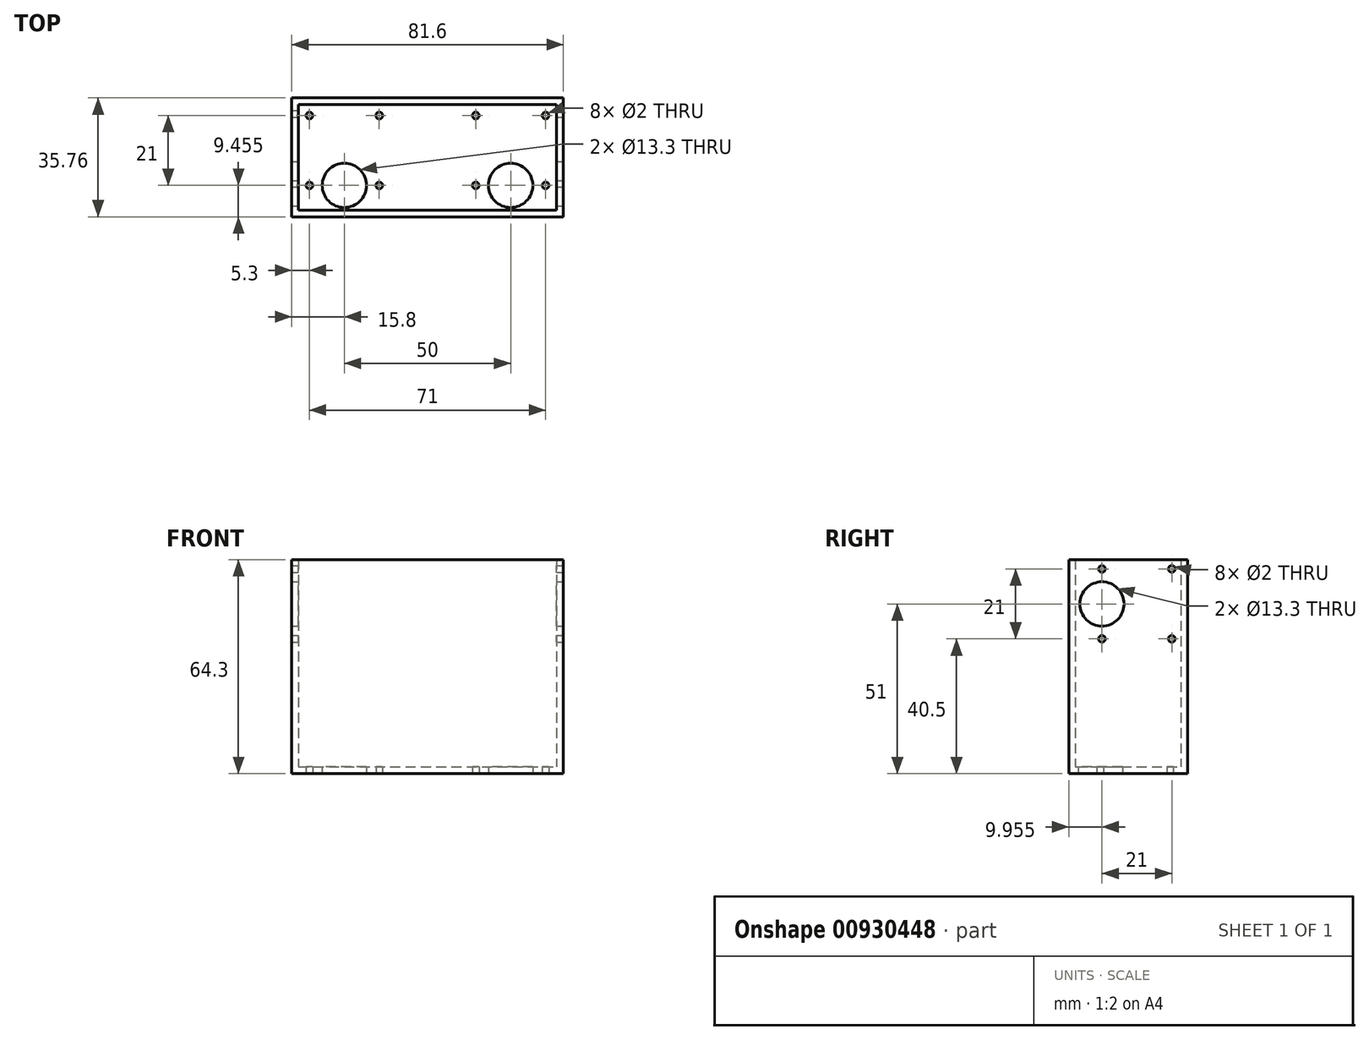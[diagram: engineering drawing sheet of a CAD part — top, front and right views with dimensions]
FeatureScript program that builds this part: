
annotation { "Feature Type Name" : "Feature", "Feature Type Description" : "" }
export const myFeature = defineFeature(function(context is Context, id is Id, definition is map)
    precondition{}
    {
        {
            var Q0;
            Q0=qCreatedBy(makeId("Top.planeOp"),FACE);
            var sketch = newSketch(context, id + "F0", { "sketchPlane" : qUnion([Q0])});
            skLineSegment(sketch, "E0.bottom", {"start": v(-40.8, 17.88) * mm, "end": v(40.8, 17.88) * mm});
            skLineSegment(sketch, "E0.top", {"start": v(-40.8, -17.88) * mm, "end": v(40.8, -17.88) * mm});
            skLineSegment(sketch, "E0.left", {"start": v(-40.8, 17.88) * mm, "end": v(-40.8, -17.88) * mm});
            skLineSegment(sketch, "E0.right", {"start": v(40.8, 17.88) * mm, "end": v(40.8, -17.88) * mm});
            skPoint(sketch, "E0.middle", {"position": v(0, 0) * mm});
            skLineSegment(sketch, "E1.bottom", {"start": v(14.5, 12.58) * mm, "end": v(35.5, 12.58) * mm, "construction": true});
            skLineSegment(sketch, "E1.top", {"start": v(14.5, -8.43) * mm, "end": v(35.5, -8.43) * mm, "construction": true});
            skLineSegment(sketch, "E1.left", {"start": v(14.5, 12.58) * mm, "end": v(14.5, -8.43) * mm, "construction": true});
            skLineSegment(sketch, "E1.right", {"start": v(35.5, 12.58) * mm, "end": v(35.5, -8.43) * mm, "construction": true});
            skPoint(sketch, "E1.middle", {"position": v(25, 2.07) * mm});
            skCircle(sketch, "E2", {"center": v(25, -8.43) * mm, "radius": 6.65 * mm});
            skPoint(sketch, "E3", {"position": v(25, -15.08) * mm});
            skCircle(sketch, "E4", {"center": v(14.5, 12.58) * mm, "radius": 1 * mm});
            skCircle(sketch, "E5.1.0", {"center": v(14.5, -8.43) * mm, "radius": 1 * mm});
            skCircle(sketch, "E5.2.0", {"center": v(35.5, -8.42) * mm, "radius": 1 * mm});
            skPoint(sketch, "E5.center", {"position": v(25, 2.08) * mm});
            skCircle(sketch, "E6.1.3.0", {"center": v(35.5, 12.58) * mm, "radius": 1 * mm});
            skCircle(sketch, "E7.MirrorC", {"center": v(-14.5, 12.58) * mm, "radius": 1 * mm});
            skCircle(sketch, "E8.MirrorC", {"center": v(-35.5, 12.58) * mm, "radius": 1 * mm});
            skCircle(sketch, "E9.MirrorC", {"center": v(-35.5, -8.42) * mm, "radius": 1 * mm});
            skCircle(sketch, "E10.MirrorC", {"center": v(-14.5, -8.43) * mm, "radius": 1 * mm});
            skCircle(sketch, "E11.MirrorC", {"center": v(-25, -8.43) * mm, "radius": 6.65 * mm});
            skLineSegment(sketch, "E12", {"start": v(-38.8, 15.87) * mm, "end": v(-38.8, -15.88) * mm});
            skLineSegment(sketch, "E13", {"start": v(-38.8, -15.88) * mm, "end": v(0, -15.88) * mm});
            skLineSegment(sketch, "E14", {"start": v(-38.8, 15.87) * mm, "end": v(0, 15.88) * mm});
            skLineSegment(sketch, "E15.MirrorCS", {"start": v(38.8, 15.87) * mm, "end": v(0, 15.88) * mm});
            skLineSegment(sketch, "E16.MirrorCS", {"start": v(38.8, 15.87) * mm, "end": v(38.8, -15.88) * mm});
            skLineSegment(sketch, "E17.MirrorCS", {"start": v(38.8, -15.88) * mm, "end": v(0, -15.88) * mm});
            skSolve(sketch);
        }
        {
            var Q0;
            Q0 = qSketchRegion(id + "F0", true);
            var Q1;
            Q1=makeQuery(id+"F0.imprint","IMPRINT",FACE,{"disambiguationData":[TD([[makeQuery(id+"F0.imprint","IMPRINT",EDGE,{"derivedFrom":sQuery(id+"F0.wireOp",EDGE,"E2")}),-1.0]])]});
            extrude(context, id + "F1", {"entities" : qUnion([Q0, Q1]), "depth" : 2 * mm, "offsetDistance" : 25 * mm});
        }
        {
            var Q0;
            Q0=makeQuery(id+"F0.imprint","IMPRINT",FACE,{"disambiguationData":[TD([[makeQuery(id+"F0.imprint","IMPRINT",EDGE,{"derivedFrom":sQuery(id+"F0.wireOp",EDGE,"E0.bottom")}),-1.0]])]});
            extrude(context, id + "F2", {"entities" : qUnion([Q0]), "operationType" : NewBodyOperationType.ADD, "depth" : (60 + 4.3) * mm, "offsetDistance" : 25 * mm});
        }
        {
            var Q0;
            {var subQ0=sQuery(id+"F0.wireOp",EDGE,"E0.right");Q0=makeQuery(id+"F2.boolean.opBoolean","MERGE",FACE,{"derivedFrom":[makeQuery(id+"F1.opExtrude","SWEPT_FACE",FACE,{"disambiguationData":[OSD([subQ0])]}),makeQuery(id+"F2.opExtrude","SWEPT_FACE",FACE,{"disambiguationData":[OSD([subQ0])]})]});}
            var sketch = newSketch(context, id + "F3", { "sketchPlane" : qUnion([Q0])});
            skLineSegment(sketch, "E18.bottom", {"start": v(-7.93, 61.5) * mm, "end": v(13.07, 61.5) * mm, "construction": true});
            skLineSegment(sketch, "E18.top", {"start": v(-7.93, 40.5) * mm, "end": v(13.08, 40.5) * mm, "construction": true});
            skLineSegment(sketch, "E18.left", {"start": v(-7.93, 61.5) * mm, "end": v(-7.93, 40.5) * mm, "construction": true});
            skLineSegment(sketch, "E18.right", {"start": v(13.07, 61.5) * mm, "end": v(13.07, 40.5) * mm, "construction": true});
            skPoint(sketch, "E18.middle", {"position": v(2.58, 51) * mm});
            skCircle(sketch, "E19", {"center": v(-7.93, 51) * mm, "radius": 6.65 * mm});
            skCircle(sketch, "E20", {"center": v(-7.93, 61.5) * mm, "radius": 1 * mm});
            skPoint(sketch, "E21", {"position": v(-14.58, 51) * mm});
            skCircle(sketch, "E22.1.0", {"center": v(-7.93, 40.5) * mm, "radius": 1 * mm});
            skCircle(sketch, "E22.2.0", {"center": v(13.08, 40.5) * mm, "radius": 1 * mm});
            skCircle(sketch, "E23.1.3.0", {"center": v(13.08, 61.5) * mm, "radius": 1 * mm});
            skSolve(sketch);
        }
        {
            var Q0;
            Q0 = qSketchRegion(id + "F3", true);
            extrude(context, id + "F4", {"entities" : qUnion([Q0]), "operationType" : NewBodyOperationType.REMOVE, "endBound" : BoundingType.THROUGH_ALL, "oppositeDirection" : true, "depth" : 25 * mm, "offsetDistance" : 25 * mm});
        }
    });
